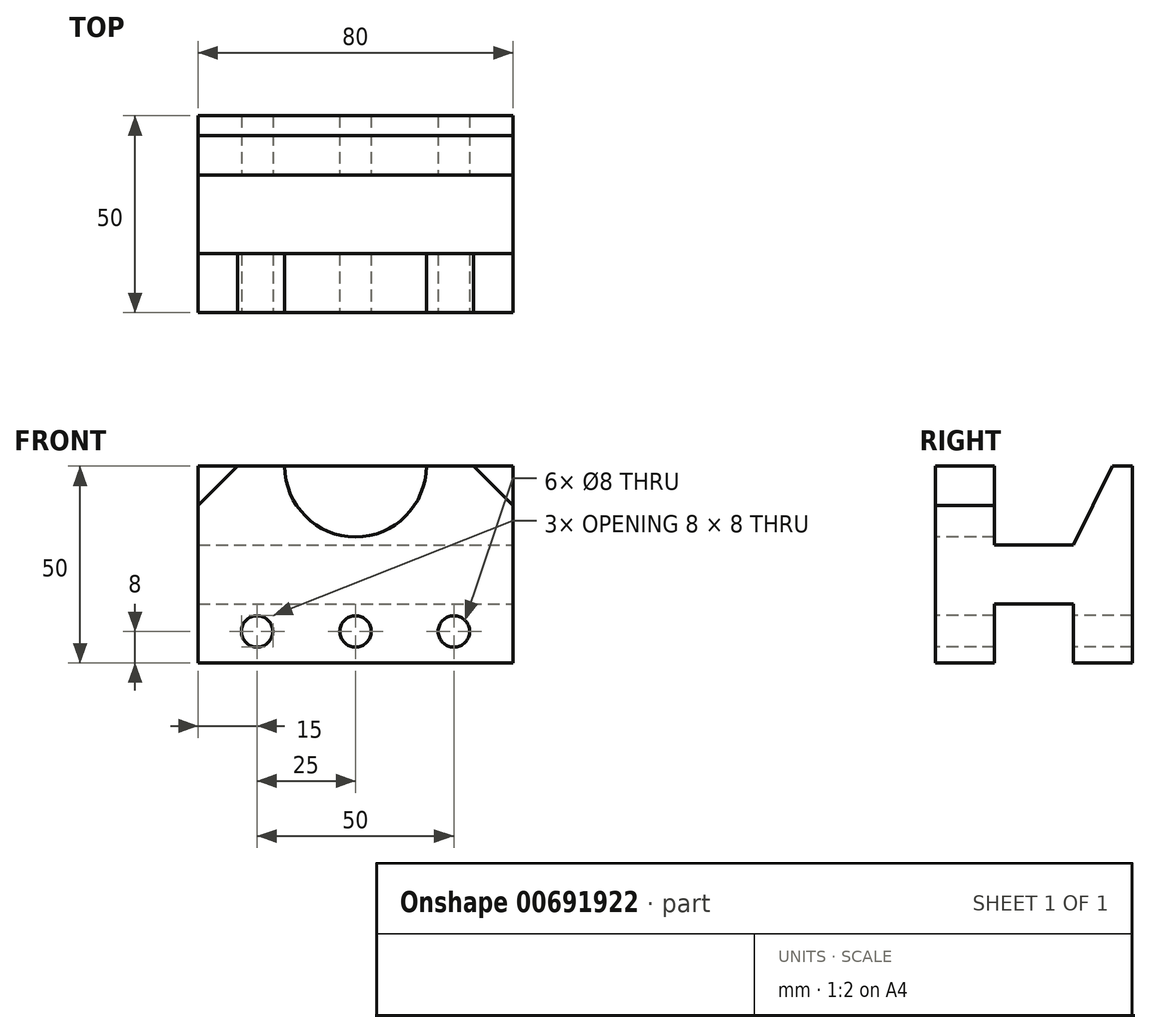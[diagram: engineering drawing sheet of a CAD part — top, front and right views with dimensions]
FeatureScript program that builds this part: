
annotation { "Feature Type Name" : "Feature", "Feature Type Description" : "" }
export const myFeature = defineFeature(function(context is Context, id is Id, definition is map)
    precondition{}
    {
        {
            var Q0;
            Q0=qCreatedBy(makeId("Front.planeOp"),FACE);
            var sketch = newSketch(context, id + "F0", { "sketchPlane" : qUnion([Q0])});
            skLineSegment(sketch, "E0.bottom", {"start": v(-40, 0) * mm, "end": v(40, 0) * mm});
            skLineSegment(sketch, "E0.top", {"start": v(-40, 50) * mm, "end": v(40, 50) * mm});
            skLineSegment(sketch, "E0.left", {"start": v(-40, 0) * mm, "end": v(-40, 50) * mm});
            skLineSegment(sketch, "E0.right", {"start": v(40, 0) * mm, "end": v(40, 50) * mm});
            skSolve(sketch);
        }
        {
            var Q0;
            Q0 = qSketchRegion(id + "F0", true);
            extrude(context, id + "F1", {"entities" : qUnion([Q0]), "depth" : 50 * mm, "offsetDistance" : 25 * mm});
        }
        {
            var Q0;
            Q0=makeQuery(id+"F1.opExtrude","SWEPT_FACE",FACE,{"disambiguationData":[OSD([sQuery(id+"F0.wireOp",EDGE,"E0.right")])]});
            var sketch = newSketch(context, id + "F2", { "sketchPlane" : qUnion([Q0])});
            skLineSegment(sketch, "E1.bottom", {"start": v(-35, 0) * mm, "end": v(-15, 0) * mm});
            skLineSegment(sketch, "E1.top", {"start": v(-35, 15) * mm, "end": v(-15, 15) * mm});
            skLineSegment(sketch, "E1.left", {"start": v(-35, 0) * mm, "end": v(-35, 15) * mm});
            skLineSegment(sketch, "E1.right", {"start": v(-15, 0) * mm, "end": v(-15, 15) * mm});
            skLineSegment(sketch, "E2", {"start": v(-35, 50) * mm, "end": v(-35, 30) * mm});
            skLineSegment(sketch, "E3", {"start": v(-35, 30) * mm, "end": v(-15, 30) * mm});
            skLineSegment(sketch, "E4", {"start": v(-15, 30) * mm, "end": v(-5, 50) * mm});
            skLineSegment(sketch, "E5", {"start": v(-35, 50) * mm, "end": v(-5, 50) * mm});
            skSolve(sketch);
        }
        {
            var Q0;
            Q0 = qSketchRegion(id + "F2", true);
            extrude(context, id + "F3", {"entities" : qUnion([Q0]), "operationType" : NewBodyOperationType.REMOVE, "endBound" : BoundingType.THROUGH_ALL, "oppositeDirection" : true, "depth" : 25 * mm, "offsetDistance" : 25 * mm});
        }
        {
            var Q0;
            Q0=makeQuery(id+"F1.opExtrude","CAP_FACE",FACE,{"disambiguationData":[OSD([sQuery(id+"F0.wireOp",EDGE,"E0.bottom"),sQuery(id+"F0.wireOp",EDGE,"E0.top"),sQuery(id+"F0.wireOp",EDGE,"E0.left"),sQuery(id+"F0.wireOp",EDGE,"E0.right")])],"isStart":false});
            var sketch = newSketch(context, id + "F4", { "sketchPlane" : qUnion([Q0])});
            skCircle(sketch, "E6", {"center": v(0, 50) * mm, "radius": 18 * mm});
            skSolve(sketch);
        }
        {
            var Q0;
            Q0 = qSketchRegion(id + "F4", true);
            var Q1;
            Q1=makeQuery(id+"F3.boolean.opBoolean","COPY",FACE,{"derivedFrom":makeQuery(id+"F3.opExtrude","SWEPT_FACE",FACE,{"disambiguationData":[OSD([sQuery(id+"F2.wireOp",EDGE,"E2")])]})});
            extrude(context, id + "F5", {"entities" : qUnion([Q0]), "operationType" : NewBodyOperationType.REMOVE, "endBound" : BoundingType.UP_TO_SURFACE, "oppositeDirection" : true, "depth" : 25 * mm, "endBoundEntityFace" : qUnion([Q1]), "offsetDistance" : 25 * mm});
        }
        {
            var Q0;
            Q0=makeQuery(id+"F1.opExtrude","CAP_FACE",FACE,{"disambiguationData":[OSD([sQuery(id+"F0.wireOp",EDGE,"E0.bottom"),sQuery(id+"F0.wireOp",EDGE,"E0.top"),sQuery(id+"F0.wireOp",EDGE,"E0.left"),sQuery(id+"F0.wireOp",EDGE,"E0.right")])],"isStart":false});
            var sketch = newSketch(context, id + "F6", { "sketchPlane" : qUnion([Q0])});
            skPoint(sketch, "E7", {"position": v(-25, 8) * mm});
            skPoint(sketch, "E8", {"position": v(0, 8) * mm});
            skPoint(sketch, "E9", {"position": v(25, 8) * mm});
            skSolve(sketch);
        }
        {
            var Q0;
            Q0=sQuery(id+"F6.wireOp",VERTEX,"E7");
            var Q1;
            Q1=sQuery(id+"F6.wireOp",VERTEX,"E8");
            var Q2;
            Q2=sQuery(id+"F6.wireOp",VERTEX,"E9");
            var Q3;
            Q3=makeQuery(id+"F1.opExtrude","SWEPT_BODY",BODY,{"disambiguationData":[OSD([sQuery(id+"F0.wireOp",EDGE,"E0.bottom"),sQuery(id+"F0.wireOp",EDGE,"E0.top"),sQuery(id+"F0.wireOp",EDGE,"E0.left"),sQuery(id+"F0.wireOp",EDGE,"E0.right")])]});
            hole(context, id + "F7", {"style" : HoleStyle.SIMPLE, "endStyle" : HoleEndStyle.THROUGH, "holeDiameter" : 8 * mm, "majorDiameter" : 5 * mm, "isTappedThrough" : true, "tappedDepth" : 12 * mm, "tapClearance" : 3, "locations" : qUnion([Q0, Q1, Q2]), "scope" : qUnion([Q3])});
        }
        {
            var Q0;
            {var subQ0=sQuery(id+"F0.wireOp",EDGE,"E0.left");var subQ1=sQuery(id+"F0.wireOp",EDGE,"E0.top");Q0=makeQuery(id+"F3.boolean.opBoolean","SPLIT",EDGE,{"disambiguationData":[TD([makeQuery(id+"F3.opExtrude","SWEPT_FACE",FACE,{"disambiguationData":[OSD([sQuery(id+"F2.wireOp",EDGE,"E2")])]})])],"derivedFrom":makeQuery(id+"F1.opExtrude","SWEPT_EDGE",EDGE,{"disambiguationData":[OSD([subQ1,subQ0])]})});}
            var Q1;
            {var subQ0=sQuery(id+"F0.wireOp",EDGE,"E0.right");var subQ1=sQuery(id+"F0.wireOp",EDGE,"E0.top");Q1=makeQuery(id+"F3.boolean.opBoolean","SPLIT",EDGE,{"disambiguationData":[TD([makeQuery(id+"F3.opExtrude","SWEPT_FACE",FACE,{"disambiguationData":[OSD([sQuery(id+"F2.wireOp",EDGE,"E2")])]})])],"derivedFrom":makeQuery(id+"F1.opExtrude","SWEPT_EDGE",EDGE,{"disambiguationData":[OSD([subQ1,subQ0])]})});}
            chamfer(context, id + "F8", {"entities" : qUnion([Q0, Q1]), "width" : 10 * mm, "tangentPropagation" : true});
        }
    });
